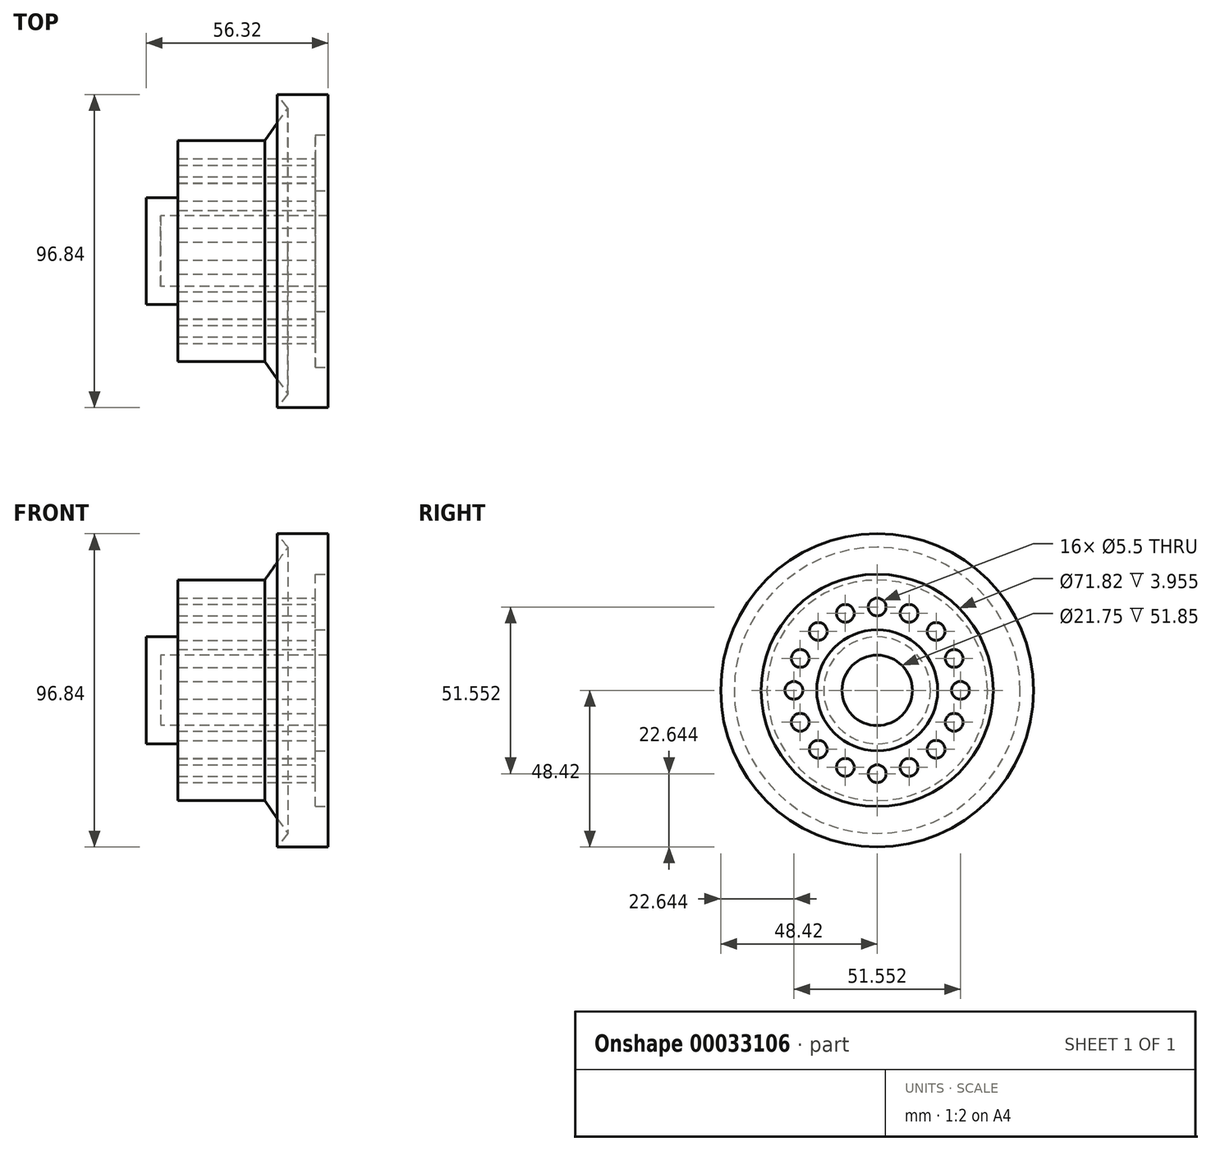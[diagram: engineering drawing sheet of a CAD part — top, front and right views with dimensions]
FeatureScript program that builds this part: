
annotation { "Feature Type Name" : "Feature", "Feature Type Description" : "" }
export const myFeature = defineFeature(function(context is Context, id is Id, definition is map)
    precondition{}
    {
        {
            var Q0;
            Q0=qCreatedBy(makeId("Front.planeOp"),FACE);
            var sketch = newSketch(context, id + "F0", { "sketchPlane" : qUnion([Q0])});
            skLineSegment(sketch, "E0", {"start": v(-51.85, 0) * mm, "end": v(-51.85, 10.88) * mm});
            skLineSegment(sketch, "E1", {"start": v(-76.28, 0) * mm, "end": v(75.95, 0) * mm});
            skLineSegment(sketch, "E2", {"start": v(-51.85, 10.88) * mm, "end": v(0, 10.88) * mm});
            skLineSegment(sketch, "E3", {"start": v(0, 10.88) * mm, "end": v(0, 48.42) * mm});
            skLineSegment(sketch, "E4", {"start": v(0, 48.42) * mm, "end": v(-15.8, 48.42) * mm});
            skLineSegment(sketch, "E5", {"start": v(-15.8, 48.42) * mm, "end": v(-12.52, 44.25) * mm});
            skLineSegment(sketch, "E6", {"start": v(-12.52, 44.25) * mm, "end": v(-19.67, 34.12) * mm});
            skLineSegment(sketch, "E7", {"start": v(-19.67, 34.12) * mm, "end": v(-46.49, 34.12) * mm});
            skLineSegment(sketch, "E8", {"start": v(-46.49, 34.12) * mm, "end": v(-46.49, 16.54) * mm});
            skLineSegment(sketch, "E9", {"start": v(-46.49, 16.54) * mm, "end": v(-56.32, 16.54) * mm});
            skLineSegment(sketch, "E10", {"start": v(-56.32, 16.54) * mm, "end": v(-56.32, 0) * mm});
            skSolve(sketch);
        }
        {
            var Q0;
            Q0 = qSketchRegion(id + "F0", true);
            var Q1;
            Q1=sQuery(id+"F0.wireOp",EDGE,"E1");
            revolve(context, id + "F1", {"entities" : qUnion([Q0]), "axis" : qUnion([Q1]), "revolveType" : RevolveType.FULL});
        }
        {
            var Q0;
            Q0=makeQuery(id+"F1.opRevolve","SWEPT_FACE",FACE,{"disambiguationData":[OSD([sQuery(id+"F0.wireOp",EDGE,"E3")])]});
            var sketch = newSketch(context, id + "F2", { "sketchPlane" : qUnion([Q0])});
            skCircle(sketch, "E11", {"center": v(0, 0) * mm, "radius": 18.7 * mm});
            skCircle(sketch, "E12", {"center": v(0, 0) * mm, "radius": 35.9 * mm});
            skSolve(sketch);
        }
        {
            var Q0;
            Q0=makeQuery(id+"F2.imprint","IMPRINT",FACE,{"disambiguationData":[TD([[makeQuery(id+"F2.imprint","IMPRINT",EDGE,{"derivedFrom":sQuery(id+"F2.wireOp",EDGE,"E11")}),-1.0]])]});
            extrude(context, id + "F3", {"entities" : qUnion([Q0]), "operationType" : NewBodyOperationType.REMOVE, "oppositeDirection" : true, "depth" : 3.96 * mm});
        }
        {
            var Q0;
            Q0=makeQuery(id+"F3.boolean.opBoolean","COPY",FACE,{"derivedFrom":makeQuery(id+"F3.opExtrude","CAP_FACE",FACE,{"disambiguationData":[OSD([sQuery(id+"F2.wireOp",EDGE,"E11"),sQuery(id+"F2.wireOp",EDGE,"E12")])],"isStart":false})});
            var sketch = newSketch(context, id + "F4", { "sketchPlane" : qUnion([Q0])});
            skCircle(sketch, "E13", {"center": v(0, 25.78) * mm, "radius": 2.75 * mm});
            skPoint(sketch, "E14.center", {"position": v(0, 0) * mm});
            skCircle(sketch, "E15.1.0", {"center": v(-9.86, 23.81) * mm, "radius": 2.75 * mm});
            skCircle(sketch, "E15.2.0", {"center": v(-18.23, 18.23) * mm, "radius": 2.75 * mm});
            skCircle(sketch, "E15.3.0", {"center": v(-23.81, 9.86) * mm, "radius": 2.75 * mm});
            skCircle(sketch, "E15.4.0", {"center": v(-25.78, 0) * mm, "radius": 2.75 * mm});
            skCircle(sketch, "E15.5.0", {"center": v(-23.81, -9.86) * mm, "radius": 2.75 * mm});
            skCircle(sketch, "E15.6.0", {"center": v(-18.23, -18.23) * mm, "radius": 2.75 * mm});
            skCircle(sketch, "E15.7.0", {"center": v(-9.86, -23.81) * mm, "radius": 2.75 * mm});
            skCircle(sketch, "E15.8.0", {"center": v(0, -25.78) * mm, "radius": 2.75 * mm});
            skCircle(sketch, "E15.9.0", {"center": v(9.86, -23.81) * mm, "radius": 2.75 * mm});
            skCircle(sketch, "E15.10.0", {"center": v(18.23, -18.23) * mm, "radius": 2.75 * mm});
            skCircle(sketch, "E15.11.0", {"center": v(23.81, -9.86) * mm, "radius": 2.75 * mm});
            skCircle(sketch, "E15.12.0", {"center": v(25.78, 0) * mm, "radius": 2.75 * mm});
            skCircle(sketch, "E15.13.0", {"center": v(23.81, 9.86) * mm, "radius": 2.75 * mm});
            skCircle(sketch, "E15.14.0", {"center": v(18.23, 18.23) * mm, "radius": 2.75 * mm});
            skCircle(sketch, "E15.15.0", {"center": v(9.86, 23.81) * mm, "radius": 2.75 * mm});
            skSolve(sketch);
        }
        {
            var Q0;
            Q0 = qSketchRegion(id + "F4", true);
            extrude(context, id + "F5", {"entities" : qUnion([Q0]), "operationType" : NewBodyOperationType.REMOVE, "oppositeDirection" : true, "depth" : 47 * mm});
        }
    });
